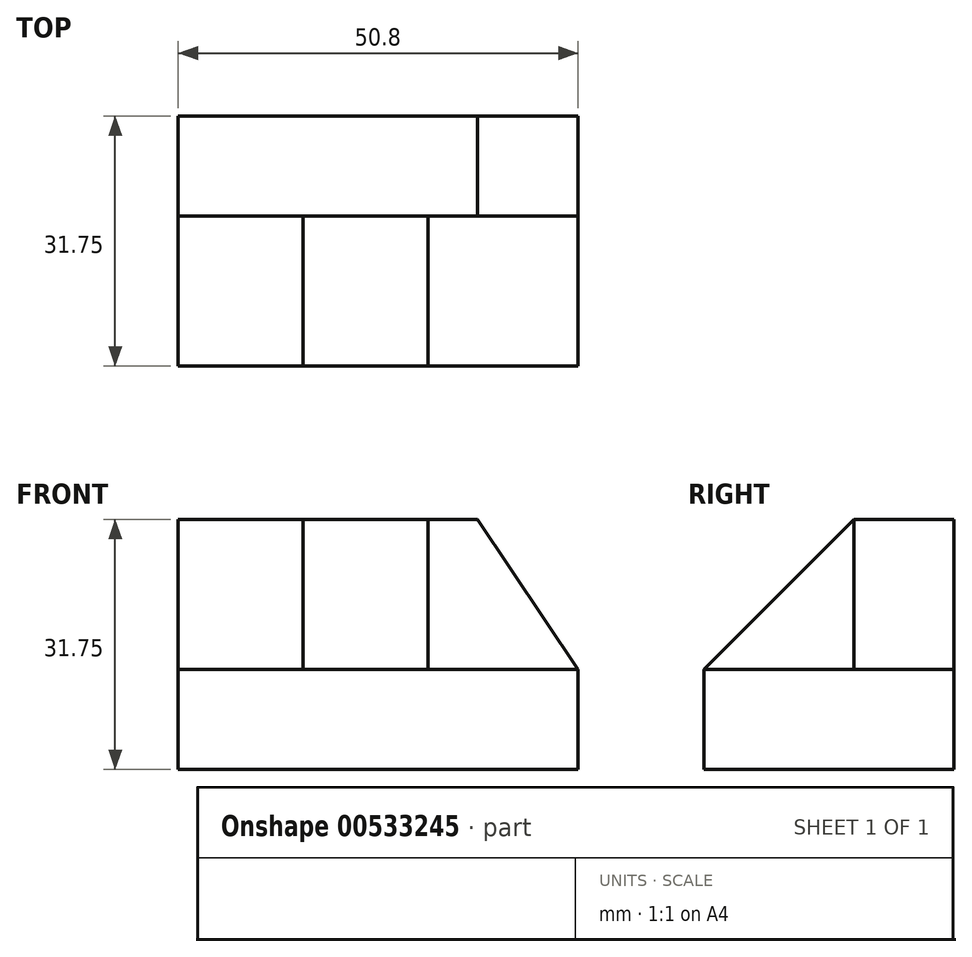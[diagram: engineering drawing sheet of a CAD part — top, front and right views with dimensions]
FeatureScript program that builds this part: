
annotation { "Feature Type Name" : "Feature", "Feature Type Description" : "" }
export const myFeature = defineFeature(function(context is Context, id is Id, definition is map)
    precondition{}
    {
        {
            var Q0;
            Q0=qCreatedBy(makeId("Right.planeOp"),FACE);
            var sketch = newSketch(context, id + "F0", { "sketchPlane" : qUnion([Q0])});
            skLineSegment(sketch, "E0.bottom", {"start": v(0, 0) * mm, "end": v(31.75, 0) * mm});
            skLineSegment(sketch, "E0.top", {"start": v(0, 31.75) * mm, "end": v(31.75, 31.75) * mm});
            skLineSegment(sketch, "E0.left", {"start": v(0, 0) * mm, "end": v(0, 31.75) * mm});
            skLineSegment(sketch, "E0.right", {"start": v(31.75, 0) * mm, "end": v(31.75, 31.75) * mm});
            skSolve(sketch);
        }
        {
            var Q0;
            Q0=makeQuery(id+"F0.imprint","IMPRINT",FACE,{"disambiguationData":[TD([[makeQuery(id+"F0.imprint","IMPRINT",EDGE,{"derivedFrom":sQuery(id+"F0.wireOp",EDGE,"E0.bottom")}),1.0]])]});
            extrude(context, id + "F1", {"entities" : qUnion([Q0]), "depth" : 50.8 * mm, "offsetDistance" : 25.4 * mm});
        }
        {
            var Q0;
            Q0=makeQuery(id+"F1.opExtrude","SWEPT_FACE",FACE,{"disambiguationData":[OSD([sQuery(id+"F0.wireOp",EDGE,"E0.left")])]});
            var sketch = newSketch(context, id + "F2", { "sketchPlane" : qUnion([Q0])});
            skLineSegment(sketch, "E1", {"start": v(50.8, 31.75) * mm, "end": v(31.75, 31.75) * mm});
            skLineSegment(sketch, "E2", {"start": v(31.75, 31.75) * mm, "end": v(31.75, 12.7) * mm});
            skLineSegment(sketch, "E3", {"start": v(31.75, 12.7) * mm, "end": v(50.8, 12.7) * mm});
            skSolve(sketch);
        }
        {
            var Q0;
            {var subQ0=sQuery(id+"F2.wireOp",EDGE,"E1");Q0=makeQuery(id+"F2.imprint","IMPRINT",FACE,{"disambiguationData":[TD([[makeQuery(id+"F2.imprint","IMPRINT",EDGE,{"derivedFrom":subQ0}),1.0]])]});}
            extrude(context, id + "F3", {"entities" : qUnion([Q0]), "operationType" : NewBodyOperationType.REMOVE, "oppositeDirection" : true, "depth" : 19.05 * mm, "offsetDistance" : 25.4 * mm});
        }
        {
            var Q0;
            Q0=makeQuery(id+"F1.opExtrude","SWEPT_FACE",FACE,{"disambiguationData":[OSD([sQuery(id+"F0.wireOp",EDGE,"E0.left")])]});
            var sketch = newSketch(context, id + "F4", { "sketchPlane" : qUnion([Q0])});
            skLineSegment(sketch, "E4", {"start": v(0, 31.75) * mm, "end": v(15.88, 31.75) * mm});
            skLineSegment(sketch, "E5", {"start": v(15.88, 31.75) * mm, "end": v(15.88, 12.7) * mm});
            skLineSegment(sketch, "E6", {"start": v(15.88, 12.7) * mm, "end": v(0, 12.7) * mm});
            skSolve(sketch);
        }
        {
            var Q0;
            {var subQ0=sQuery(id+"F4.wireOp",EDGE,"E4");Q0=makeQuery(id+"F4.imprint","IMPRINT",FACE,{"disambiguationData":[TD([[makeQuery(id+"F4.imprint","IMPRINT",EDGE,{"derivedFrom":subQ0}),1.0]])]});}
            extrude(context, id + "F5", {"entities" : qUnion([Q0]), "operationType" : NewBodyOperationType.REMOVE, "oppositeDirection" : true, "depth" : 19.05 * mm, "offsetDistance" : 25.4 * mm});
        }
        {
            var Q0;
            Q0=makeQuery(id+"F3.boolean.opBoolean","COPY",FACE,{"derivedFrom":makeQuery(id+"F3.opExtrude","SWEPT_FACE",FACE,{"disambiguationData":[OSD([sQuery(id+"F2.wireOp",EDGE,"E2")])]})});
            var sketch = newSketch(context, id + "F6", { "sketchPlane" : qUnion([Q0])});
            skLineSegment(sketch, "E7", {"start": v(0, 12.7) * mm, "end": v(19.05, 31.75) * mm});
            skSolve(sketch);
        }
        {
            var Q0;
            Q0=makeQuery(id+"F6.imprint","IMPRINT",FACE,{"disambiguationData":[TD([[makeQuery(id+"F6.imprint","IMPRINT",EDGE,{"derivedFrom":sQuery(id+"F6.wireOp",EDGE,"E7")}),1.0]])]});
            extrude(context, id + "F7", {"entities" : qUnion([Q0]), "operationType" : NewBodyOperationType.REMOVE, "oppositeDirection" : true, "depth" : 25.4 * mm, "offsetDistance" : 25.4 * mm});
        }
        {
            var Q0;
            Q0=makeQuery(id+"F3.boolean.opBoolean","COPY",FACE,{"derivedFrom":makeQuery(id+"F3.opExtrude","CAP_FACE",FACE,{"disambiguationData":[OSD([sQuery(id+"F0.wireOp",EDGE,"E0.left"),sQuery(id+"F2.wireOp",EDGE,"E1"),sQuery(id+"F2.wireOp",EDGE,"E2"),sQuery(id+"F2.wireOp",EDGE,"E3")])],"isStart":false})});
            var sketch = newSketch(context, id + "F8", { "sketchPlane" : qUnion([Q0])});
            skLineSegment(sketch, "E8", {"start": v(50.8, 31.75) * mm, "end": v(37.99, 31.75) * mm});
            skLineSegment(sketch, "E9", {"start": v(37.99, 31.75) * mm, "end": v(50.8, 12.7) * mm});
            skSolve(sketch);
        }
        {
            var Q0;
            Q0=makeQuery(id+"F8.imprint","IMPRINT",FACE,{"disambiguationData":[TD([[makeQuery(id+"F8.imprint","IMPRINT",EDGE,{"derivedFrom":sQuery(id+"F8.wireOp",EDGE,"E8")}),1.0]])]});
            extrude(context, id + "F9", {"entities" : qUnion([Q0]), "operationType" : NewBodyOperationType.REMOVE, "oppositeDirection" : true, "depth" : 12.7 * mm, "offsetDistance" : 25.4 * mm});
        }
    });
